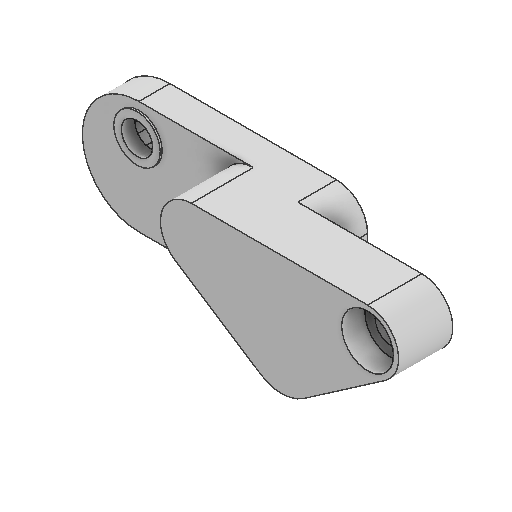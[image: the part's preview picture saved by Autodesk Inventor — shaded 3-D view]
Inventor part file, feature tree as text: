
AUTODESK INVENTOR PART (.ipt)
format: ipt  version: 2025 (Build 290162000, 162)  size: 251,392 bytes
history: native  units: mm
features: extrude x12, sketch x12, projected_geometry x10, fillet x1, thicken_offset x1
ambient origin geometry x8: Origin, YZ Plane, XZ Plane, XY Plane, X Axis, Y Axis, Z Axis, Center Point
bodies: Solid1 (feature_tree)
feature tree (36):
  extrude  "Extrusion1"  Depth=8.0mm
  extrude  "Extrusion2"  Depth=10.0mm TaperAngle=0.0deg
  extrude  "Extrusion3"  Depth=10.0mm TaperAngle=0.0deg
  extrude  "Extrusion4"  Depth=10.0mm
  fillet  "Fillet1"  Radius=2.0mm
  extrude  "Extrusion5"  Depth=0.5mm TaperAngle=0.0deg
  extrude  "Extrusion6"  Depth=10.0mm TaperAngle=0.0deg
  extrude  "Extrusion7"  Depth=2.0mm TaperAngle=0.0deg
  extrude  "Extrusion8"  Depth=13.0mm
  extrude  "Extrusion9"  [1 undecoded]
  extrude  "Extrusion10"  [1 undecoded]
  extrude  "Extrusion11"  [1 undecoded]
  thicken_offset  "Thicken1"
  extrude  "Extrusion12"  [1 undecoded]
  sketch  "Sketch1"  dims[d0=75.0mm d1=8.0mm]
  sketch  "Sketch2"  dims[d2=8.1mm d3=10.0mm d4=0.0mm]
  projected_geometry  "Projected Loop1"
  sketch  "Sketch3"  dims[d5=10.0mm d6=0.0mm d7=10.0mm d8=0.0mm]
  projected_geometry  "Projected Loop2"
  sketch  "Sketch4"  dims[d9=10.0mm d10=0.0mm d11=10.0mm d12=2.0mm d13=0.0mm]
  projected_geometry  "Projected Loop3"
  sketch  "Sketch5"  dims[d14=5.0mm d15=0.0mm d16=0.5mm d17=0.0mm]
  projected_geometry  "Projected Loop4"
  sketch  "Sketch6"  dims[d18=0.5mm d19=0.0mm d20=10.0mm d21=0.0mm]
  sketch  "Sketch7"  dims[d22=10.0mm d23=0.0mm d24=2.0mm d25=0.0mm]
  projected_geometry  "Projected Loop5"
  sketch  "Sketch8"  dims[d26=4.0mm d27=2.0mm d28=13.0mm]
  projected_geometry  "Projected Loop6"
  sketch  "Sketch9"  dims[d29=0.0mm d30=0.0mm]
  projected_geometry  "Projected Loop7"
  sketch  "Sketch10"
  projected_geometry  "Projected Loop8"
  projected_geometry  "Projected Loop9"
  sketch  "Sketch11"
  projected_geometry  "Projected Loop10"
  sketch  "Sketch12"
note: 4 required parameter values undecoded (feature->parameter linkage not recoverable at this tier; creation-order binding heuristic only, values carry confidence <= 0.55)
